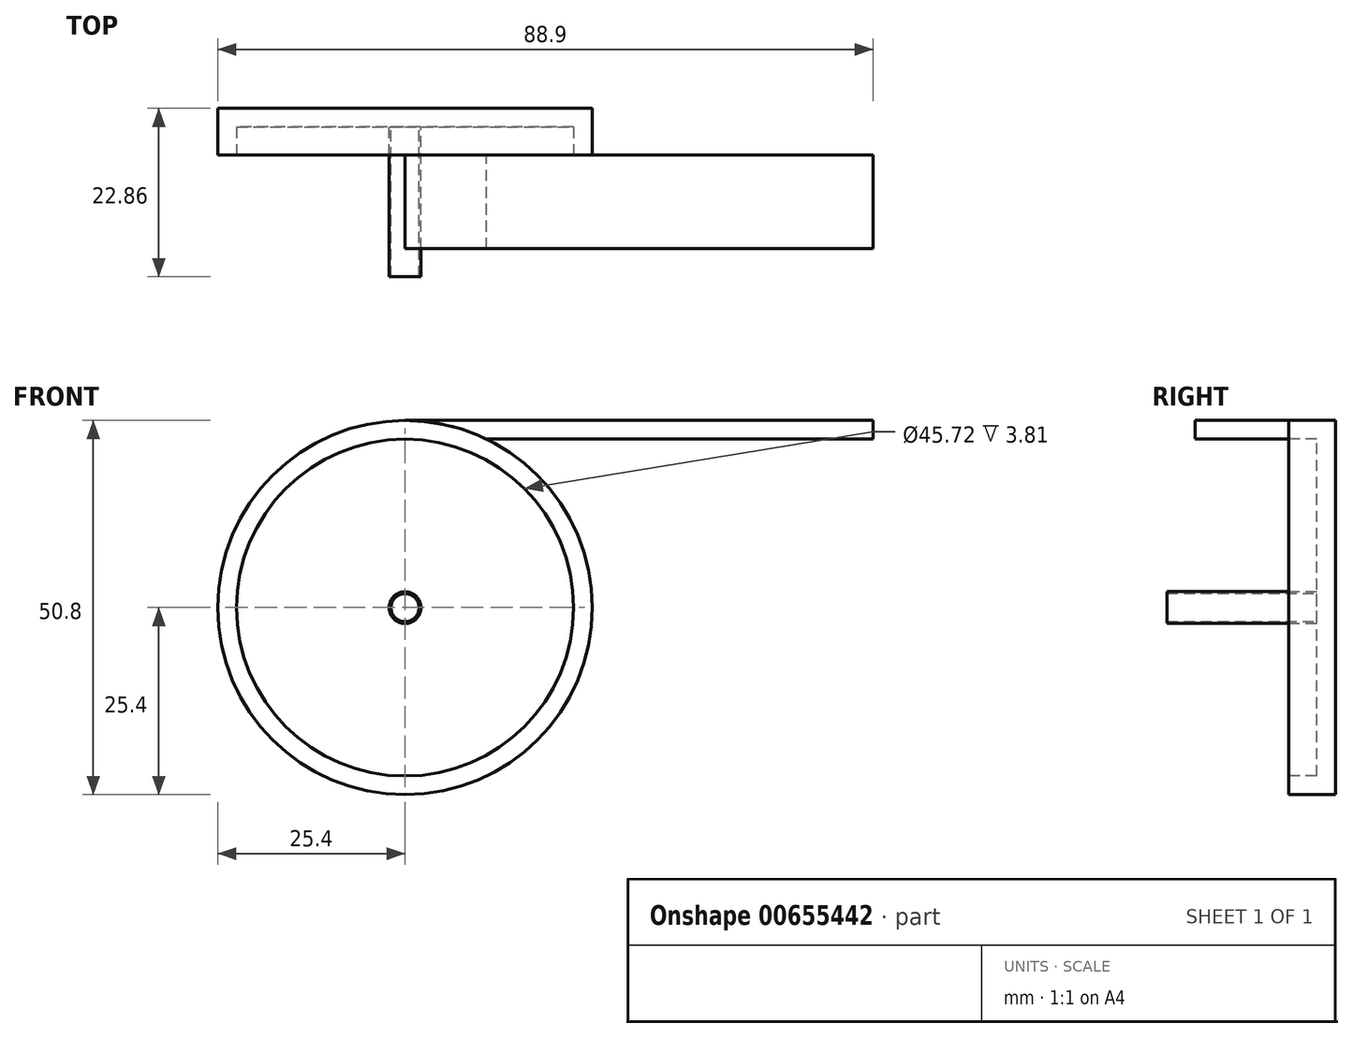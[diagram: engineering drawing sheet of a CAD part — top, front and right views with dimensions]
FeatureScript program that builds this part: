
annotation { "Feature Type Name" : "Feature", "Feature Type Description" : "" }
export const myFeature = defineFeature(function(context is Context, id is Id, definition is map)
    precondition{}
    {
        {
            var Q0;
            Q0=qCreatedBy(makeId("Front.planeOp"),FACE);
            var sketch = newSketch(context, id + "F0", { "sketchPlane" : qUnion([Q0])});
            skCircle(sketch, "E0", {"center": v(0, 0) * mm, "radius": 25.4 * mm});
            skLineSegment(sketch, "E1", {"start": v(0, 0) * mm, "end": v(0, 25.4) * mm});
            skLineSegment(sketch, "E2", {"start": v(0, 25.4) * mm, "end": v(101.6, 25.4) * mm});
            skCircle(sketch, "E3", {"center": v(0, 0) * mm, "radius": 22.86 * mm});
            skSolve(sketch);
        }
        {
            var Q0;
            Q0=makeQuery(id+"F0.imprint","IMPRINT",FACE,{"disambiguationData":[TD([[makeQuery(id+"F0.imprint","IMPRINT",EDGE,{"derivedFrom":sQuery(id+"F0.wireOp",EDGE,"E0")}),1.0]])]});
            extrude(context, id + "F1", {"entities" : qUnion([Q0]), "oppositeDirection" : true, "depth" : 3.8 * mm, "offsetDistance" : 25.4 * mm});
        }
        {
            var Q0;
            Q0=makeQuery(id+"F1.opExtrude","CAP_FACE",FACE,{"disambiguationData":[OSD([sQuery(id+"F0.wireOp",EDGE,"E0"),sQuery(id+"F0.wireOp",EDGE,"E3")])],"isStart":false});
            var sketch = newSketch(context, id + "F2", { "sketchPlane" : qUnion([Q0])});
            skCircle(sketch, "E4", {"center": v(0, 0) * mm, "radius": 25.4 * mm});
            skSolve(sketch);
        }
        {
            var Q0;
            Q0 = qSketchRegion(id + "F2", true);
            extrude(context, id + "F3", {"entities" : qUnion([Q0]), "operationType" : NewBodyOperationType.ADD, "depth" : 2.54 * mm, "offsetDistance" : 25.4 * mm});
        }
        {
            var Q0;
            Q0=makeQuery(id+"F1.opExtrude","CAP_FACE",FACE,{"disambiguationData":[OSD([sQuery(id+"F0.wireOp",EDGE,"E0"),sQuery(id+"F0.wireOp",EDGE,"E3")])],"isStart":true});
            var sketch = newSketch(context, id + "F4", { "sketchPlane" : qUnion([Q0])});
            skLineSegment(sketch, "E5", {"start": v(0, 22.86) * mm, "end": v(0, 25.4) * mm});
            skLineSegment(sketch, "E6", {"start": v(0, 25.4) * mm, "end": v(63.5, 25.4) * mm});
            skLineSegment(sketch, "E7", {"start": v(0, 22.86) * mm, "end": v(63.5, 22.86) * mm});
            skLineSegment(sketch, "E8", {"start": v(63.5, 25.4) * mm, "end": v(63.5, 22.86) * mm});
            skSolve(sketch);
        }
        {
            var Q0;
            {var subQ0=sQuery(id+"F4.wireOp",EDGE,"E6");Q0=makeQuery(id+"F4.imprint","IMPRINT",FACE,{"disambiguationData":[TD([[makeQuery(id+"F4.imprint","IMPRINT",EDGE,{"derivedFrom":subQ0}),-1.0]])]});}
            extrude(context, id + "F5", {"entities" : qUnion([Q0]), "depth" : 12.7 * mm, "offsetDistance" : 25.4 * mm});
        }
        {
            var Q0;
            Q0=makeQuery(id+"F3.opExtrude","CAP_FACE",FACE,{"disambiguationData":[OSD([sQuery(id+"F2.wireOp",EDGE,"E4")])],"isStart":true});
            var sketch = newSketch(context, id + "F6", { "sketchPlane" : qUnion([Q0])});
            skCircle(sketch, "E9", {"center": v(0, 0) * mm, "radius": 1.9 * mm});
            skSolve(sketch);
        }
        {
            var Q0;
            Q0=makeQuery(id+"F6.imprint","IMPRINT",FACE,{"disambiguationData":[TD([[makeQuery(id+"F6.imprint","IMPRINT",EDGE,{"derivedFrom":sQuery(id+"F6.wireOp",EDGE,"E9")}),1.0]])]});
            var Q1;
            Q1=sQuery(id+"F6.wireOp",EDGE,"E9");
            extrude(context, id + "F7", {"entities" : qUnion([Q0]), "surfaceEntities" : qUnion([Q1]), "depth" : 20.32 * mm, "offsetDistance" : 25.4 * mm});
        }
        {
            var Q0;
            Q0=makeQuery(id+"F3.opExtrude","CAP_FACE",FACE,{"disambiguationData":[OSD([sQuery(id+"F2.wireOp",EDGE,"E4")])],"isStart":true});
            var sketch = newSketch(context, id + "F8", { "sketchPlane" : qUnion([Q0])});
            skCircle(sketch, "E10", {"center": v(0, 0) * mm, "radius": 2.16 * mm});
            skSolve(sketch);
        }
        {
            var Q0;
            Q0=makeQuery(id+"F8.imprint","IMPRINT",FACE,{"disambiguationData":[TD([[makeQuery(id+"F8.imprint","IMPRINT",EDGE,{"derivedFrom":sQuery(id+"F8.wireOp",EDGE,"E10")}),1.0]])]});
            var Q1;
            Q1=sQuery(id+"F8.wireOp",EDGE,"E10");
            extrude(context, id + "F9", {"entities" : qUnion([Q0]), "surfaceEntities" : qUnion([Q1]), "depth" : 20.32 * mm, "offsetDistance" : 25.4 * mm});
        }
    });
